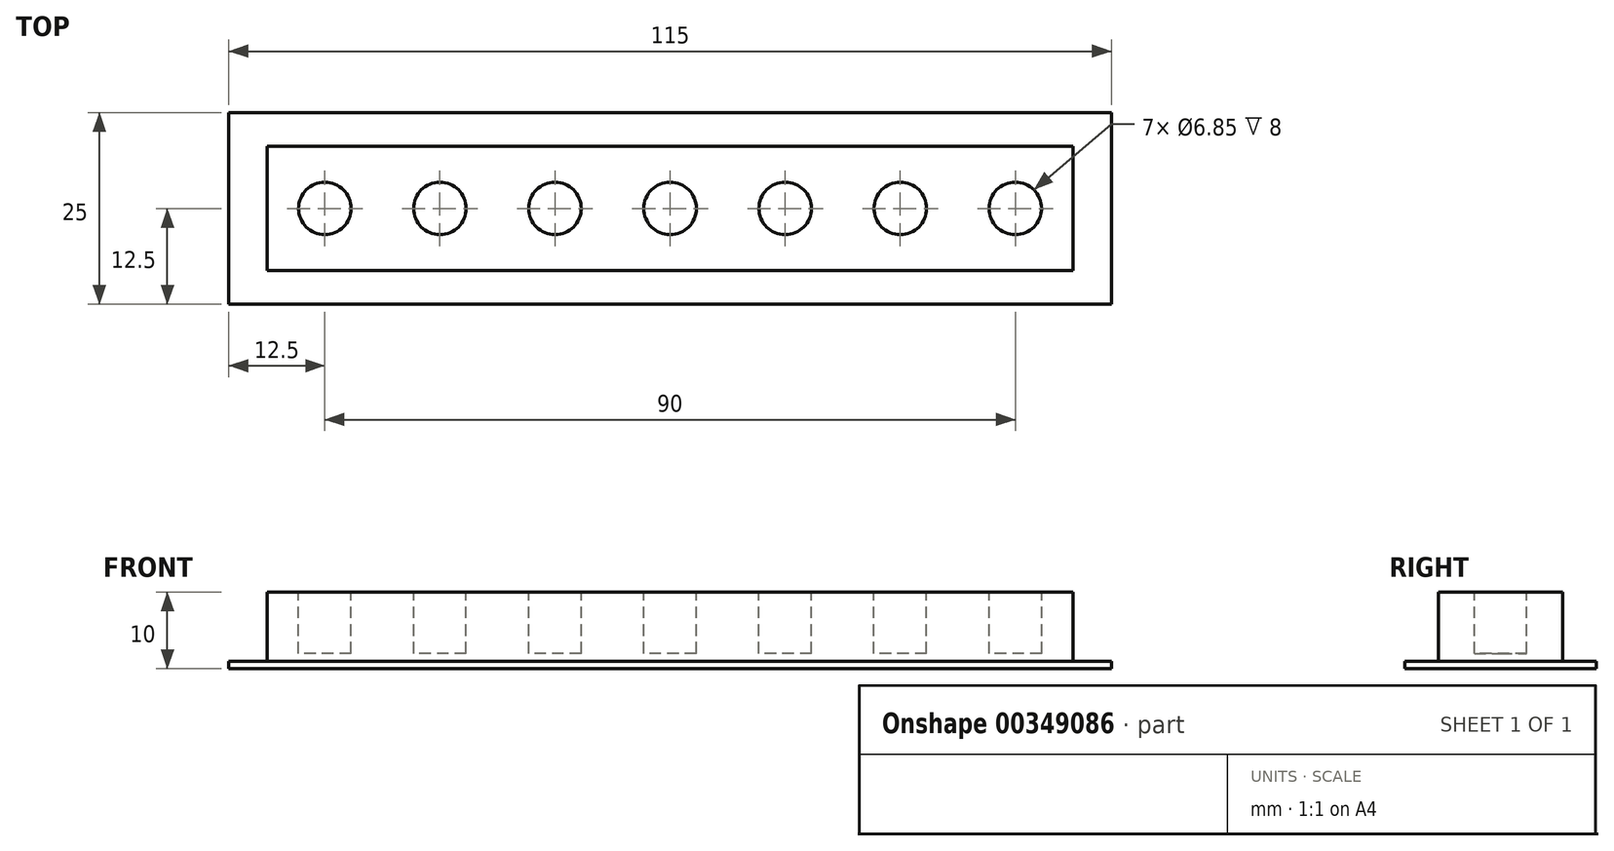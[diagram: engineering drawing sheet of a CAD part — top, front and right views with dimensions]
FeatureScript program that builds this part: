
annotation { "Feature Type Name" : "Feature", "Feature Type Description" : "" }
export const myFeature = defineFeature(function(context is Context, id is Id, definition is map)
    precondition{}
    {
        {
            assignVariable(context, id + "F0", {"name" : "foot_height", "anyValue" : 1});
        }
        {
            assignVariable(context, id + "F1", {"name" : "hole_depth", "anyValue" : 8});
        }
        {
            var Q0;
            Q0=qCreatedBy(makeId("Top.planeOp"),FACE);
            var sketch = newSketch(context, id + "F2", { "sketchPlane" : qUnion([Q0])});
            skLineSegment(sketch, "E0.bottom", {"start": v(57.5, 12.5) * mm, "end": v(-57.5, 12.5) * mm});
            skLineSegment(sketch, "E0.top", {"start": v(57.5, -12.5) * mm, "end": v(-57.5, -12.5) * mm});
            skLineSegment(sketch, "E0.left", {"start": v(57.5, 12.5) * mm, "end": v(57.5, -12.5) * mm});
            skLineSegment(sketch, "E0.right", {"start": v(-57.5, 12.5) * mm, "end": v(-57.5, -12.5) * mm});
            skPoint(sketch, "E0.middle", {"position": v(0, 0) * mm});
            skSolve(sketch);
        }
        {
            var Q0;
            Q0=makeQuery(id+"F2.imprint","IMPRINT",FACE,{"disambiguationData":[TD([[makeQuery(id+"F2.imprint","IMPRINT",EDGE,{"derivedFrom":sQuery(id+"F2.wireOp",EDGE,"E0.bottom")}),1.0]])]});
            extrude(context, id + "F3", {"entities" : qUnion([Q0]), "depth" : (getVariable(context, 'foot_height')) * mm});
        }
        {
            var Q0;
            Q0=makeQuery(id+"F3.opExtrude","CAP_FACE",FACE,{"disambiguationData":[OSD([sQuery(id+"F2.wireOp",EDGE,"E0.bottom"),sQuery(id+"F2.wireOp",EDGE,"E0.top"),sQuery(id+"F2.wireOp",EDGE,"E0.left"),sQuery(id+"F2.wireOp",EDGE,"E0.right")])],"isStart":false});
            var sketch = newSketch(context, id + "F4", { "sketchPlane" : qUnion([Q0])});
            skLineSegment(sketch, "E1.bottom", {"start": v(52.5, -8.07) * mm, "end": v(-52.5, -8.07) * mm});
            skLineSegment(sketch, "E1.top", {"start": v(52.5, 8.07) * mm, "end": v(-52.5, 8.07) * mm});
            skLineSegment(sketch, "E1.left", {"start": v(52.5, -8.07) * mm, "end": v(52.5, 8.07) * mm});
            skLineSegment(sketch, "E1.right", {"start": v(-52.5, -8.07) * mm, "end": v(-52.5, 8.07) * mm});
            skPoint(sketch, "E1.middle", {"position": v(0, 0) * mm});
            skSolve(sketch);
        }
        {
            var Q0;
            Q0=makeQuery(id+"F4.imprint","IMPRINT",FACE,{"disambiguationData":[TD([[makeQuery(id+"F4.imprint","IMPRINT",EDGE,{"derivedFrom":sQuery(id+"F4.wireOp",EDGE,"E1.bottom")}),-1.0]])]});
            extrude(context, id + "F5", {"entities" : qUnion([Q0]), "operationType" : NewBodyOperationType.ADD, "depth" : (getVariable(context, 'hole_depth') + 1) * mm});
        }
        {
            var Q0;
            Q0=makeQuery(id+"F5.opExtrude","CAP_FACE",FACE,{"disambiguationData":[OSD([sQuery(id+"F4.wireOp",EDGE,"E1.bottom"),sQuery(id+"F4.wireOp",EDGE,"E1.top"),sQuery(id+"F4.wireOp",EDGE,"E1.left"),sQuery(id+"F4.wireOp",EDGE,"E1.right")])],"isStart":false});
            var sketch = newSketch(context, id + "F6", { "sketchPlane" : qUnion([Q0])});
            skCircle(sketch, "E2", {"center": v(0, 0) * mm, "radius": 3.43 * mm});
            skLineSegment(sketch, "E3", {"start": v(0, 0) * mm, "end": v(15, 0) * mm, "construction": true});
            skLineSegment(sketch, "E4", {"start": v(15, 0) * mm, "end": v(30, 0) * mm, "construction": true});
            skLineSegment(sketch, "E5", {"start": v(30, 0) * mm, "end": v(45, 0) * mm, "construction": true});
            skLineSegment(sketch, "E6", {"start": v(0, 0) * mm, "end": v(-15, 0) * mm, "construction": true});
            skLineSegment(sketch, "E7", {"start": v(-15, 0) * mm, "end": v(-30, 0) * mm, "construction": true});
            skLineSegment(sketch, "E8", {"start": v(-30, 0) * mm, "end": v(-45, 0) * mm, "construction": true});
            skCircle(sketch, "E9", {"center": v(-15, 0) * mm, "radius": 3.43 * mm});
            skCircle(sketch, "E10", {"center": v(-30, 0) * mm, "radius": 3.43 * mm});
            skCircle(sketch, "E11", {"center": v(-45, 0) * mm, "radius": 3.43 * mm});
            skCircle(sketch, "E12", {"center": v(15, 0) * mm, "radius": 3.43 * mm});
            skCircle(sketch, "E13", {"center": v(30, 0) * mm, "radius": 3.43 * mm});
            skCircle(sketch, "E14", {"center": v(45, 0) * mm, "radius": 3.43 * mm});
            skSolve(sketch);
        }
        {
            var Q0;
            Q0=makeQuery(id+"F6.imprint","IMPRINT",FACE,{"disambiguationData":[TD([[makeQuery(id+"F6.imprint","IMPRINT",EDGE,{"derivedFrom":sQuery(id+"F6.wireOp",EDGE,"E11")}),1.0]])]});
            var Q1;
            Q1=makeQuery(id+"F6.imprint","IMPRINT",FACE,{"disambiguationData":[TD([[makeQuery(id+"F6.imprint","IMPRINT",EDGE,{"derivedFrom":sQuery(id+"F6.wireOp",EDGE,"E10")}),1.0]])]});
            var Q2;
            Q2=makeQuery(id+"F6.imprint","IMPRINT",FACE,{"disambiguationData":[TD([[makeQuery(id+"F6.imprint","IMPRINT",EDGE,{"derivedFrom":sQuery(id+"F6.wireOp",EDGE,"E9")}),1.0]])]});
            var Q3;
            Q3=makeQuery(id+"F6.imprint","IMPRINT",FACE,{"disambiguationData":[TD([[makeQuery(id+"F6.imprint","IMPRINT",EDGE,{"derivedFrom":sQuery(id+"F6.wireOp",EDGE,"E2")}),1.0]])]});
            var Q4;
            Q4=makeQuery(id+"F6.imprint","IMPRINT",FACE,{"disambiguationData":[TD([[makeQuery(id+"F6.imprint","IMPRINT",EDGE,{"derivedFrom":sQuery(id+"F6.wireOp",EDGE,"E12")}),1.0]])]});
            var Q5;
            Q5=makeQuery(id+"F6.imprint","IMPRINT",FACE,{"disambiguationData":[TD([[makeQuery(id+"F6.imprint","IMPRINT",EDGE,{"derivedFrom":sQuery(id+"F6.wireOp",EDGE,"E13")}),1.0]])]});
            var Q6;
            Q6=makeQuery(id+"F6.imprint","IMPRINT",FACE,{"disambiguationData":[TD([[makeQuery(id+"F6.imprint","IMPRINT",EDGE,{"derivedFrom":sQuery(id+"F6.wireOp",EDGE,"E14")}),1.0]])]});
            extrude(context, id + "F7", {"entities" : qUnion([Q0, Q1, Q2, Q3, Q4, Q5, Q6]), "operationType" : NewBodyOperationType.REMOVE, "oppositeDirection" : true, "depth" : (getVariable(context, 'hole_depth')) * mm});
        }
    });
